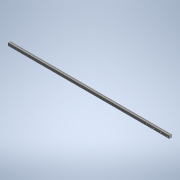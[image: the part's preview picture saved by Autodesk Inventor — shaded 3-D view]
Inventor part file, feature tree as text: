
AUTODESK INVENTOR PART (.ipt)
format: ipt  version: 2022 (Build 260153000, 153)  size: 164,352 bytes
history: native  units: mm (DEFAULTED — no unit token found)
features: other x21, sketch x2, extrude x1, hole x1, pattern_linear x1
ambient origin geometry x8: Origin, YZ Plane, XZ Plane, XY Plane, X Axis, Y Axis, Z Axis, Center Point
bodies: Solid1 (feature_tree)
feature tree (26):
  extrude  "Extrusion1"  Depth=10.0mm TaperAngle=0.0deg
  hole  "Hole1"  [1 undecoded]
  pattern_linear  "Rectangular Pattern1"  Spacing1=0.5mm  [1 undecoded]
  other  "4dummy_XY"
  other  "4dummy_YZ"
  other  "4dummy_ZX"
  other  "4dummy_X"
  other  "4dummy_Y"
  other  "4dummy_Z"
  other  "4dummy_Center"
  other  "4slide_XY"
  other  "4slide_YZ"
  other  "4slide_ZX"
  other  "4slide_X"
  other  "4slide_Y"
  other  "4slide_Z"
  other  "4slide_Center"
  other  "4track_XY"
  other  "4track_YZ"
  other  "4track_ZX"
  other  "4track_X"
  other  "4track_Y"
  other  "4track_Z"
  other  "4track_Center"
  sketch  "Sketch_18"  dims[d2=9.0mm d3=6.0mm d4=14.0mm d5=12.0mm d6=90.0deg d7=29.0mm d8=0.0mm d9=40.0mm d11=80.0mm d12=10.0mm d14=0.0mm d15=0.0mm d16=0.5mm d17=0.872665mm d18=0.5mm d19=0.872665mm]
  sketch  "Sketch2"  dims[d0=1828.8mm d1=0.0mm]
note: 2 required parameter values undecoded (feature->parameter linkage not recoverable at this tier; creation-order binding heuristic only, values carry confidence <= 0.55)
